# Revit family: DOP36M94D_Revit
name_source: partatom
category: Specialty Equipment
revit_build: Autodesk Revit MEP 2014 (Build: 20130308_1515(x64)
units: mm (PartAtom-declared; Revit-internal decimal feet)

## types (1)
- DOP36M94D
    AMBIENTLIGHTING = YES (DIMMING)
    Adjustment = Stainless Steel
    BAKE ELEMENT = 3,000W - 8 PASS
    BLACK BURNER CAPS = YES
    BLUETOOTH (HOOD CONNECTION) = YES
    BRASS BURNER CAPS = YES
    BROIL ELEMENT = 4,400W - 10 PASS
    Burner = Plastic-Black
    CAVITY = BLACK ENAMEL COATING
    CHILD LOCK = YES
    CIRCUIT BREAKER (A) = 50
    CLEANING TYPE = SELF CLEAN & GREENCLEAN
    CLOCK = YES
    CONTROL METHOD = 7” POP-UP LCD
    CONVECTION ELEMENT = 1,300W (EACH - 2,600W TOTAL)
    CONVECTION FILTER = 2
    CONVECTION TYPE = FOUR PART DUAL PURE CONVECTION WITH FILTER
    COOKIE SHEETS (SET OF 3) = SKU - ACSM303
    COOKING MODES = BAKE - BROIL - CONVECTION BAKE - CONVECTION ROAST - CONVECTION BROIL - FOUR PART PURE CONVECTION - PURE CONVECTION SEAR - STEAM ASSIST
    DELAY START = YES
    Depth = 24"
    Description = 36-INCH PRO DUAL-FUEL STEAM RANGE MODERNIST COLLECTION
    Door = Stainless Steel
    ENERGY SOURCE = GAS AND ELECTRIC
    FREQUENCY (HZ) = 60
    GAS TYPE = NATURAL GAS NATURAL GAS (HIGH ALTITUDE) LIQUID PROPANE LIQUID PROPANE (HIGH ALTITU
    GLIDERACK™ = GLIDERACK™
    Gas Burner = Stainless Steel
    Glide = Plastic-Black
    HIGHLIGHTING COLOR = WHITE
    Handle = Stainless Steel
    Height = 37 1/2"
    ILLULMINA™ BURNER KNOBS = YES / WHITE
    INFOCENTER™ DISPLAY = YES
    KITCHEN TIMER = YES
    LEFT FRONT (BTU) = 18,000 DUAL (SIMMER)
    LEFT REAR (BTU) = 16,000 DUAL (SIMMER)
    LIGHTING = BRIGHTVUE™ - LED + HALOGEN
    LIMITED, PARTS AND LABOR = 1 YEAR
    MANUAL LIGHTING ON/OFF = YES
    Manufacturer = Dacor
    Model = DOP36M94D
    NUMBER OF KNOBS = 5 + 1 LAMP KNOBS
    OVEN CAPACITY (CUBIC FEET) = 4.8
    PERMA-FLAME™ (AUTO RE-IGNITION) = YES
    POWER OF GRIDDLE = 1,400 W
    RACK POSITIONS = 6
    RIGHT FRONT (BTU) = 22,000 DUAL (SIMMER)
    RIGHT REAR (BTU) = 9,000 STACK DUAL (SIMMER)
    SEALED BURNERS = YES
    SOUND ON/OFF = YES
    STANDARD RACKS = 1
    STEAM HEATER = 500W
    Support = Glass
    TEMPERATURE (F / C) = YES
    TEMPERATURE PROBE = 1
    TIME OF DAY (12 HR/24 HR) = YES
    TOTAL NUMBER OF COOKTOP BURNERS = 4 + GRIDDLE
    TYPE OF GRATE = CONTINUOUS CAST IRON
    Unit = Stainless Steel
    VOLTS (V) = 240 / 208
    WI FI = YES
    WOK RING = 1
    Width = 35 7/8"

## geometry (parser evidence)
native form markers: Blend x2, Sweep x3
no freeform markers — native parametric forms only
